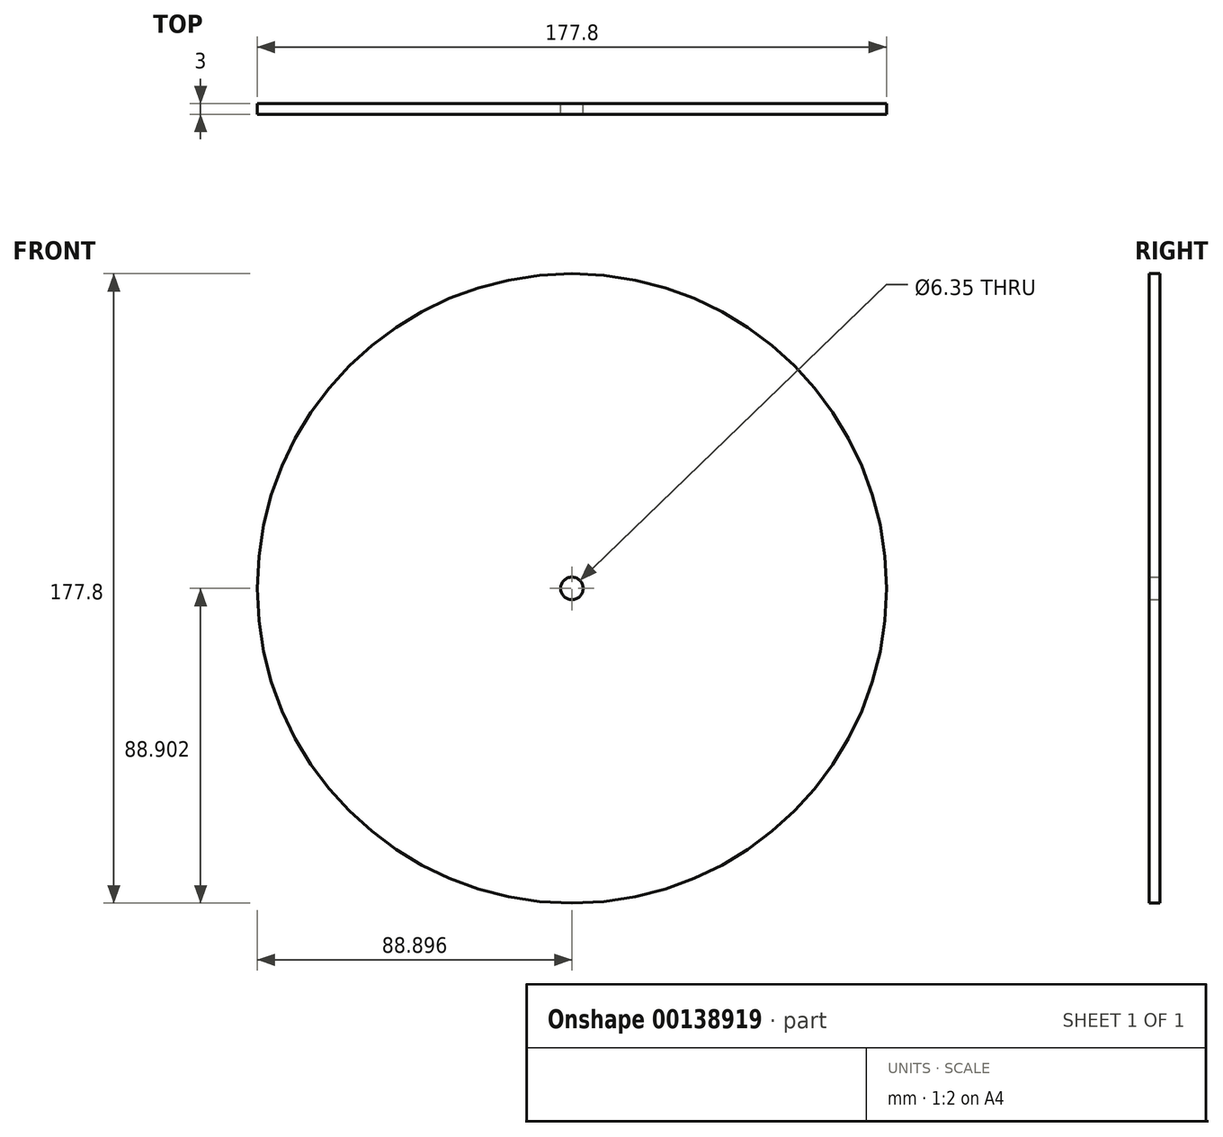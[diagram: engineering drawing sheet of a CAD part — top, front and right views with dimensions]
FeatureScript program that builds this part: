
annotation { "Feature Type Name" : "Feature", "Feature Type Description" : "" }
export const myFeature = defineFeature(function(context is Context, id is Id, definition is map)
    precondition{}
    {
        {
            var Q0;
            Q0=qCreatedBy(makeId("Front.planeOp"),FACE);
            var sketch = newSketch(context, id + "F0", { "sketchPlane" : qUnion([Q0])});
            skCircle(sketch, "E0", {"center": v(-90.01, -3.23) * mm, "radius": 88.9 * mm});
            skCircle(sketch, "E1", {"center": v(-90.01, -3.23) * mm, "radius": 3.18 * mm});
            skSolve(sketch);
        }
        {
            var Q0;
            Q0=makeQuery(id+"F0.imprint","IMPRINT",FACE,{"disambiguationData":[TD([[makeQuery(id+"F0.imprint","IMPRINT",EDGE,{"derivedFrom":sQuery(id+"F0.wireOp",EDGE,"E0")}),1.0]])]});
            extrude(context, id + "F1", {"entities" : qUnion([Q0]), "depth" : 3 * mm});
        }
    });
